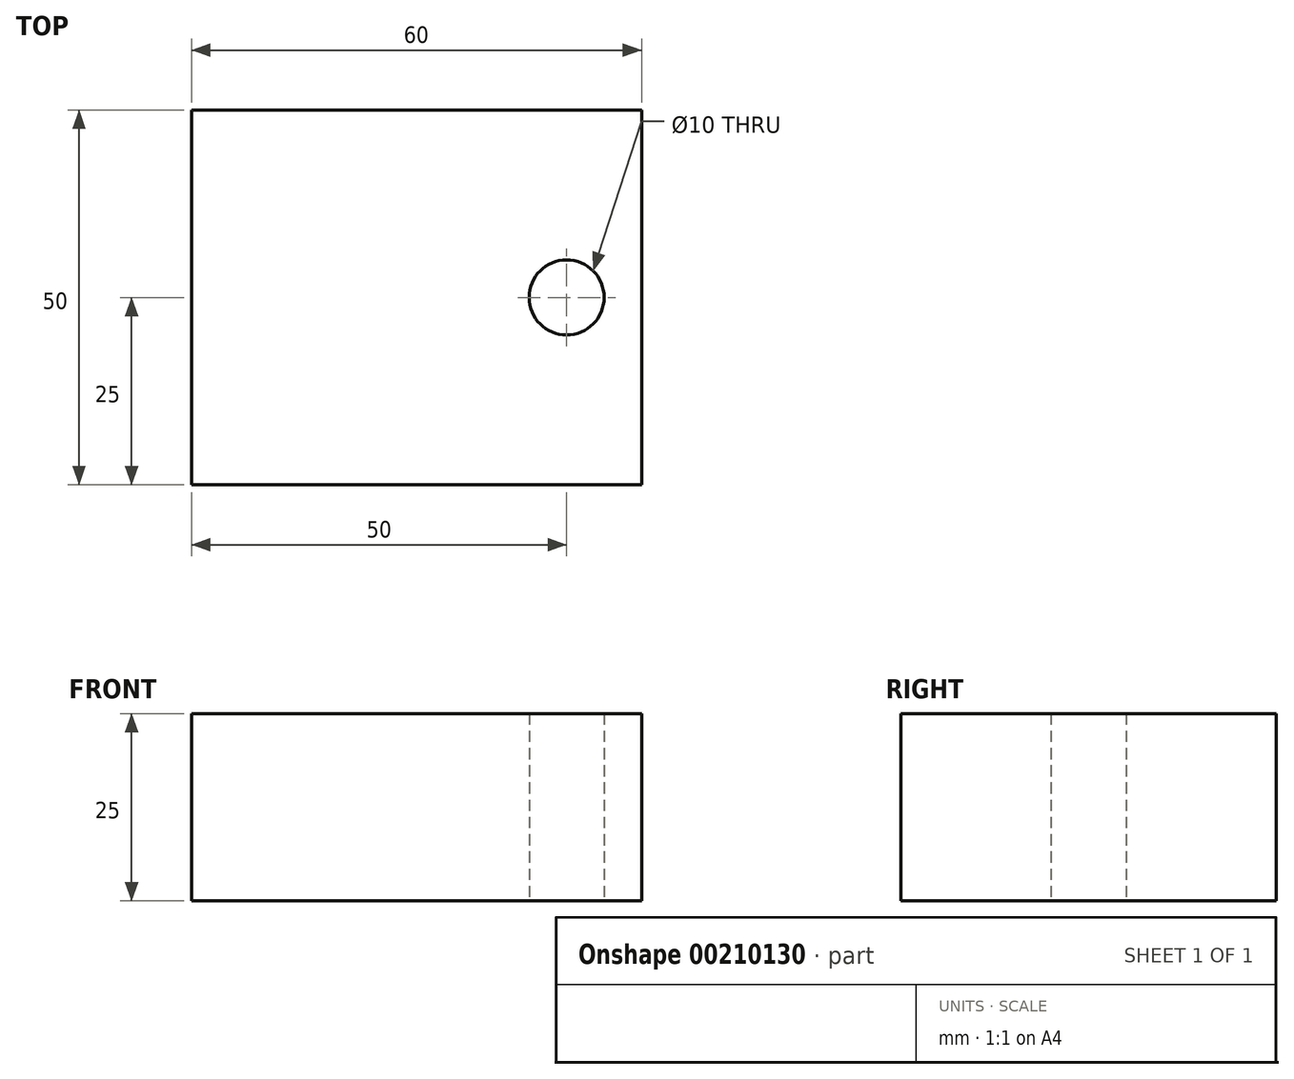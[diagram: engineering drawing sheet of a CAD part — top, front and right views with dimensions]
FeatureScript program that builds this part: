
annotation { "Feature Type Name" : "Feature", "Feature Type Description" : "" }
export const myFeature = defineFeature(function(context is Context, id is Id, definition is map)
    precondition{}
    {
        {
            var Q0;
            Q0=qCreatedBy(makeId("Top.planeOp"),FACE);
            var sketch = newSketch(context, id + "F0", { "sketchPlane" : qUnion([Q0])});
            skLineSegment(sketch, "E0.bottom", {"start": v(-30, 25) * mm, "end": v(30, 25) * mm});
            skLineSegment(sketch, "E0.top", {"start": v(-30, -25) * mm, "end": v(30, -25) * mm});
            skLineSegment(sketch, "E0.left", {"start": v(-30, 25) * mm, "end": v(-30, -25) * mm});
            skLineSegment(sketch, "E0.right", {"start": v(30, 25) * mm, "end": v(30, -25) * mm});
            skPoint(sketch, "E0.middle", {"position": v(0, 0) * mm});
            skCircle(sketch, "E1", {"center": v(20, 0) * mm, "radius": 5 * mm});
            skLineSegment(sketch, "E2", {"start": v(20, 0) * mm, "end": v(30, 0) * mm, "construction": true});
            skSolve(sketch);
        }
        {
            var Q0;
            Q0 = qSketchRegion(id + "F0", true);
            extrude(context, id + "F1", {"entities" : qUnion([Q0]), "depth" : 25 * mm});
        }
    });
